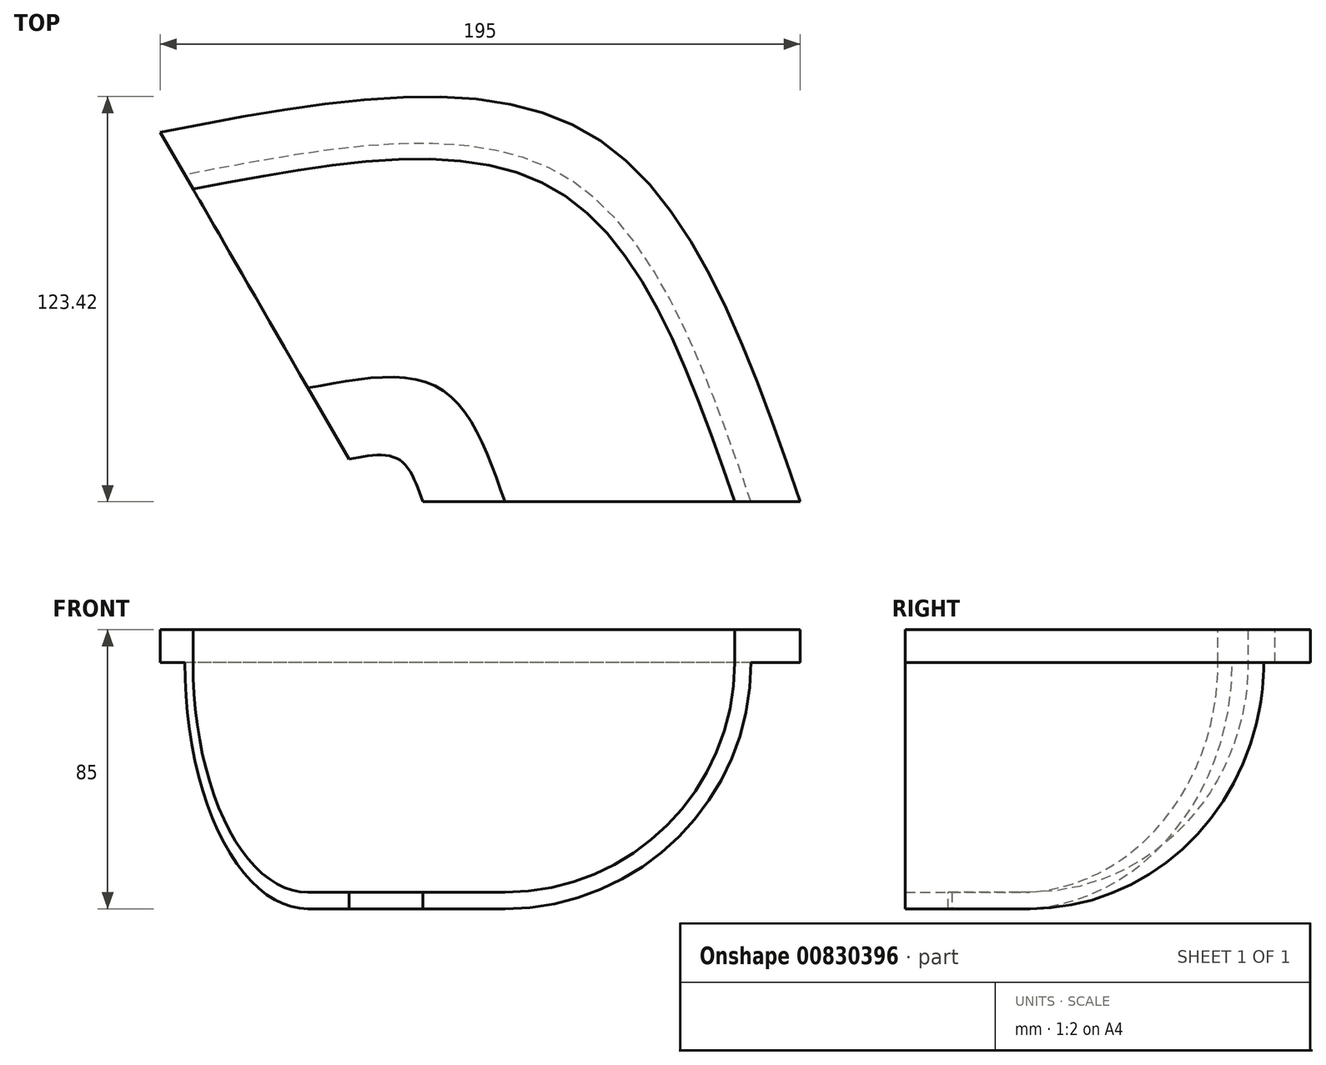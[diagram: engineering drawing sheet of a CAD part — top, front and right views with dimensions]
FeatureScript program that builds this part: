
annotation { "Feature Type Name" : "Feature", "Feature Type Description" : "" }
export const myFeature = defineFeature(function(context is Context, id is Id, definition is map)
    precondition{}
    {
        {
            var Q0;
            Q0=qCreatedBy(makeId("Front.planeOp"),FACE);
            var sketch = newSketch(context, id + "F0", { "sketchPlane" : qUnion([Q0])});
            skLineSegment(sketch, "E0.bottom", {"start": v(40, 0) * mm, "end": v(15, 0) * mm});
            skLineSegment(sketch, "E0.top", {"start": v(40, 5) * mm, "end": v(15, 5) * mm});
            skLineSegment(sketch, "E0.right", {"start": v(15, 0) * mm, "end": v(15, 5) * mm});
            skPoint(sketch, "E0.middle", {"position": v(27.5, 2.5) * mm});
            skLineSegment(sketch, "E1.bottom", {"start": v(130, 75) * mm, "end": v(115, 75) * mm});
            skLineSegment(sketch, "E1.top", {"start": v(130, 85) * mm, "end": v(110, 85) * mm});
            skLineSegment(sketch, "E1.left", {"start": v(130, 75) * mm, "end": v(130, 85) * mm});
            skLineSegment(sketch, "E1.right", {"start": v(110, 75) * mm, "end": v(110, 85) * mm});
            skPoint(sketch, "E1.middle", {"position": v(120, 80) * mm});
            skArc(sketch, "E2", {"start": v(40, 0) * mm, "mid": v(93.03, 21.97) * mm, "end": v(115, 75) * mm});
            skArc(sketch, "E3", {"start": v(40, 5) * mm, "mid": v(89.5, 25.5) * mm, "end": v(110, 75) * mm});
            skLineSegment(sketch, "E4", {"start": v(40, 5) * mm, "end": v(40, 0) * mm, "construction": true});
            skLineSegment(sketch, "E5", {"start": v(0, 0) * mm, "end": v(0, 75.18) * mm, "construction": true});
            skSolve(sketch);
        }
        {
            var Q0;
            Q0=sQuery(id+"F0.wireOp",EDGE,"E5");
            cPlane(context, id + "F1", {"entities" : qUnion([Q0]), "cplaneType" : CPlaneType.LINE_ANGLE, "offset" : 25 * mm, "angle" : 30 * degree, "width" : 150 * mm, "height" : 150 * mm});
        }
        {
            var Q0;
            Q0=qCreatedBy(id+"F1.planeOp",FACE);
            var sketch = newSketch(context, id + "F2", { "sketchPlane" : qUnion([Q0])});
            skLineSegment(sketch, "E6.bottom", {"start": v(40, 0) * mm, "end": v(15, 0) * mm});
            skLineSegment(sketch, "E6.top", {"start": v(40, 5) * mm, "end": v(15, 5) * mm});
            skLineSegment(sketch, "E6.right", {"start": v(15, 0) * mm, "end": v(15, 5) * mm});
            skPoint(sketch, "E6.middle", {"position": v(27.5, 2.5) * mm});
            skLineSegment(sketch, "E7.bottom", {"start": v(130, 75) * mm, "end": v(115, 75) * mm});
            skLineSegment(sketch, "E7.top", {"start": v(130, 85) * mm, "end": v(110, 85) * mm});
            skLineSegment(sketch, "E7.left", {"start": v(130, 75) * mm, "end": v(130, 85) * mm});
            skLineSegment(sketch, "E7.right", {"start": v(110, 75) * mm, "end": v(110, 85) * mm});
            skPoint(sketch, "E7.middle", {"position": v(120, 80) * mm});
            skArc(sketch, "E8", {"start": v(40, 0) * mm, "mid": v(93.03, 21.97) * mm, "end": v(115, 75) * mm});
            skArc(sketch, "E9", {"start": v(40, 5) * mm, "mid": v(89.5, 25.5) * mm, "end": v(110, 75) * mm});
            skLineSegment(sketch, "E10", {"start": v(40, 5) * mm, "end": v(40, 0) * mm, "construction": true});
            skLineSegment(sketch, "E11", {"start": v(0, 0) * mm, "end": v(0, 75.18) * mm, "construction": true});
            skSolve(sketch);
        }
        {
            var Q0;
            Q0=sQuery(id+"F2.wireOp",EDGE,"E11");
            cPlane(context, id + "F3", {"entities" : qUnion([Q0]), "cplaneType" : CPlaneType.LINE_ANGLE, "offset" : 25 * mm, "angle" : 30 * degree, "oppositeDirection" : true, "width" : 150 * mm, "height" : 150 * mm});
        }
        {
            var Q0;
            Q0=qCreatedBy(id+"F3.planeOp",FACE);
            var sketch = newSketch(context, id + "F4", { "sketchPlane" : qUnion([Q0])});
            skLineSegment(sketch, "E12.bottom", {"start": v(40, 0) * mm, "end": v(15, 0) * mm});
            skLineSegment(sketch, "E12.top", {"start": v(40, 5) * mm, "end": v(15, 5) * mm});
            skLineSegment(sketch, "E12.right", {"start": v(15, 0) * mm, "end": v(15, 5) * mm});
            skPoint(sketch, "E12.middle", {"position": v(27.5, 2.5) * mm});
            skLineSegment(sketch, "E13.bottom", {"start": v(130, 75) * mm, "end": v(115, 75) * mm});
            skLineSegment(sketch, "E13.top", {"start": v(130, 85) * mm, "end": v(110, 85) * mm});
            skLineSegment(sketch, "E13.left", {"start": v(130, 75) * mm, "end": v(130, 85) * mm});
            skLineSegment(sketch, "E13.right", {"start": v(110, 75) * mm, "end": v(110, 85) * mm});
            skPoint(sketch, "E13.middle", {"position": v(120, 80) * mm});
            skArc(sketch, "E14", {"start": v(40, 0) * mm, "mid": v(93.03, 21.97) * mm, "end": v(115, 75) * mm});
            skArc(sketch, "E15", {"start": v(40, 5) * mm, "mid": v(89.5, 25.5) * mm, "end": v(110, 75) * mm});
            skLineSegment(sketch, "E16", {"start": v(40, 5) * mm, "end": v(40, 0) * mm, "construction": true});
            skLineSegment(sketch, "E17", {"start": v(0, 0) * mm, "end": v(0, 75.18) * mm, "construction": true});
            skSolve(sketch);
        }
        {
            var Q0;
            Q0 = qSketchRegion(id + "F0", true);
            var Q1;
            Q1 = qSketchRegion(id + "F4", true);
            var Q2;
            Q2 = qSketchRegion(id + "F2", true);
            loft(context, id + "F5", {"sheetProfilesArray" : [{ "sheetProfileEntities" : qUnion([Q0]) }, { "sheetProfileEntities" : qUnion([Q1]) }, { "sheetProfileEntities" : qUnion([Q2]) }]});
        }
    });
